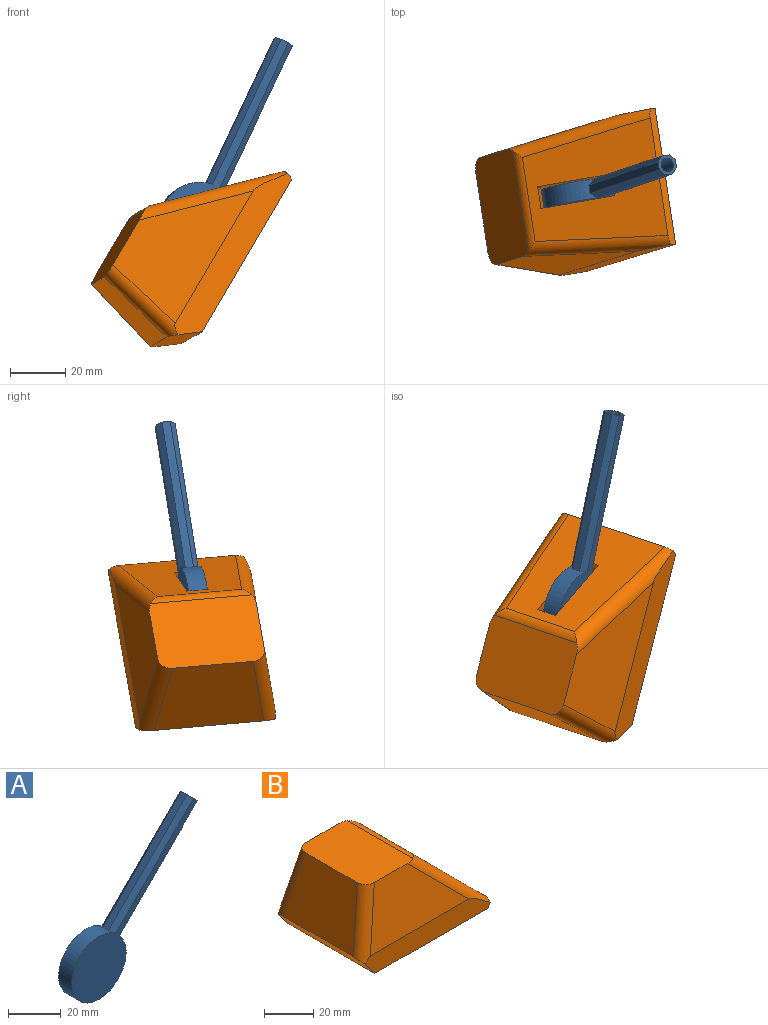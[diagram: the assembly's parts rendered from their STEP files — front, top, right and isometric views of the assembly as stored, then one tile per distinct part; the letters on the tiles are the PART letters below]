
ASSEMBLY  parts=2 mates=1
PART A: 12 faces, bbox 68.5x7x69.1 mm
  f0: cylinder r=14.5mm len=29mm, axis (0,-1,0), area 596.4mm2, adj f1,f2,f3,f4,f6,f7,f8,f9
  f1: plane 67.66x67.04mm, normal (0,1,0), area 836.8mm2, adj f0,f5,f7,f8
  f2: plane 67.66x67.04mm, normal (0,-1,0), area 836.8mm2, adj f0,f5,f6,f9
  f3: plane 41.92x41.92mm, normal (-0.71,0,0.71), area 177.9mm2, adj f0,f5,f6,f7
  f4: plane 41.77x41.77mm, normal (0.71,0,-0.71), area 177.2mm2, adj f0,f5,f8,f9
  f5: plane 7x4.95mm, normal (0.71,0,0.71), area 21.4mm2, adj f1,f2,f3,f4,f6,f7,f8,f9
  f6: plane 43.35x43.06mm, normal (-0.5,-0.71,0.5), area 167mm2, adj f0,f2,f3,f5
  f7: plane 43.35x43.06mm, normal (-0.5,0.71,0.5), area 167mm2, adj f0,f1,f3,f5
  f8: plane 43.19x42.99mm, normal (0.5,0.71,-0.5), area 166.6mm2, adj f0,f1,f4,f5
  f9: plane 43.19x42.99mm, normal (0.5,-0.71,-0.5), area 166.6mm2, adj f0,f2,f4,f5
  f10: cylinder r=2.5mm len=10.61mm, axis (0.71,0,0.71), area 157.1mm2, adj f5,f11
  f11: plane 5x3.54mm, normal (0.71,0,0.71), area 19.6mm2, adj f10
PART B: 22 faces, bbox 75.3x53.4x42.7 mm
  f0: cylinder r=14.5mm len=26.14mm, axis (0,1,0), area 398.5mm2, adj f16,f17,f18,f19
  f1: plane 71.5x10mm, normal (0,1,0), area 651.4mm2, adj f4,f7,f9,f11,f14,f15
  f2: plane 71.5x10mm, normal (0,-1,0), area 651.4mm2, adj f4,f6,f10,f13,f14,f15
  f3: plane 39.42x27.93mm, normal (0,0,1), area 1088.1mm2, adj f6,f7,f8,f9,f10,f11,f12,f13
  f4: plane 65x50mm, normal (0,0,-1), area 3221.7mm2, adj f1,f2,f14,f15,f20
  f5: plane 43.37x35mm, normal (0.71,0,0.71), area 1618.4mm2, adj f11,f12,f13,f15,f16,f17,f18,f19
  f6: plane 56.36x30mm, normal (0,-0.98,0.17), area 1145.7mm2, adj f2,f3,f10,f13
  f7: plane 56.36x30mm, normal (0,0.98,0.17), area 1145.7mm2, adj f1,f3,f9,f11
  f8: plane 40.38x30.3mm, normal (-0.97,0,0.24), area 1094.2mm2, adj f3,f9,f10,f14
  f9: cylinder r=5mm len=33.94mm, axis (-0.24,0.17,-0.96), area 248.9mm2, adj f1,f3,f7,f8,f14
  f10: cylinder r=5mm len=33.94mm, axis (-0.24,-0.17,-0.96), area 248.9mm2, adj f2,f3,f6,f8,f14
  f11: cylinder r=5mm len=43.3mm, axis (-0.7,-0.12,0.7), area 354.8mm2, adj f1,f3,f5,f7,f12,f15
  f12: cylinder r=5mm len=37.27mm, axis (0,-1,0), area 134.8mm2, adj f3,f5,f11,f13
  f13: cylinder r=5mm len=43.3mm, axis (-0.7,0.12,0.7), area 354.8mm2, adj f2,f3,f5,f6,f12,f15
  f14: plane 50x9.7mm, normal (-0.79,0,-0.62), area 605.7mm2, adj f1,f2,f4,f8,f9,f10
  f15: plane 50x3.54mm, normal (0.92,0,-0.38), area 188.6mm2, adj f1,f2,f4,f5,f11,f13
  f16: plane 30.18x30.18mm, normal (0,1,0), area 567.4mm2, adj f0,f5,f18,f19
  f17: plane 30.18x30.18mm, normal (0,-1,0), area 567.4mm2, adj f0,f5,f18,f19
  f18: cylinder r=14.5mm len=8mm, axis (0,1,0), area 49.5mm2, adj f0,f5,f16,f17
  f19: cylinder r=14.5mm len=8mm, axis (0,1,0), area 49.5mm2, adj f0,f5,f16,f17
  f20: cylinder r=3mm len=6mm, axis (0,0,-1), area 94.2mm2, adj f4,f21
  f21: plane 6x6mm, normal (0,0,-1), area 28.3mm2, adj f20
PLACE A rot(axis=(-0.16,-0.89,0.43),21.6deg) t=(-40.03,18.43,-17.75)mm
PLACE B rot(axis=(0,-0.98,0.17),60deg) t=(-26.59,21.47,-12.11)mm
MATE revolute A.f0 <-> B.f16  axis (0.15,-0.98,0.09) through (-38.69,16.96,3.98)mm
